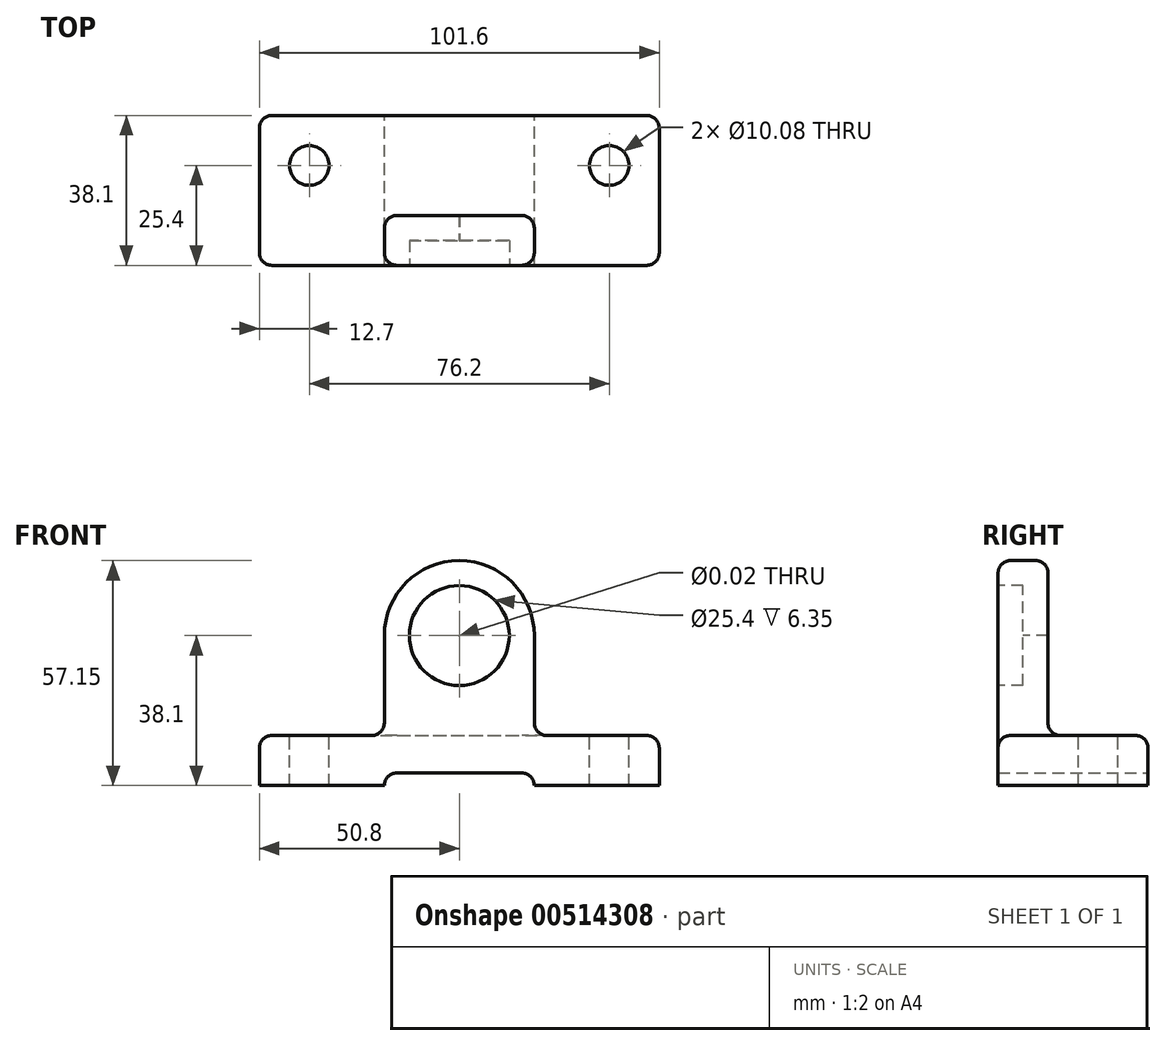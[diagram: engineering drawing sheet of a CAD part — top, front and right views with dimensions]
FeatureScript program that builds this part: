
annotation { "Feature Type Name" : "Feature", "Feature Type Description" : "" }
export const myFeature = defineFeature(function(context is Context, id is Id, definition is map)
    precondition{}
    {
        {
            var Q0;
            Q0=qCreatedBy(makeId("Top.planeOp"),FACE);
            var sketch = newSketch(context, id + "F0", { "sketchPlane" : qUnion([Q0])});
            skLineSegment(sketch, "E0.bottom", {"start": v(0, 0) * mm, "end": v(101.6, 0) * mm});
            skLineSegment(sketch, "E0.top", {"start": v(0, 38.1) * mm, "end": v(101.6, 38.1) * mm});
            skLineSegment(sketch, "E0.left", {"start": v(0, 0) * mm, "end": v(0, 38.1) * mm});
            skLineSegment(sketch, "E0.right", {"start": v(101.6, 0) * mm, "end": v(101.6, 38.1) * mm});
            skSolve(sketch);
        }
        {
            var Q0;
            Q0=makeQuery(id+"F0.imprint","IMPRINT",FACE,{"disambiguationData":[TD([[makeQuery(id+"F0.imprint","IMPRINT",EDGE,{"derivedFrom":sQuery(id+"F0.wireOp",EDGE,"E0.bottom")}),1.0]])]});
            extrude(context, id + "F1", {"entities" : qUnion([Q0]), "depth" : 12.7 * mm, "offsetDistance" : 25.4 * mm});
        }
        {
            var Q0;
            Q0=makeQuery(id+"F1.opExtrude","SWEPT_FACE",FACE,{"disambiguationData":[OSD([sQuery(id+"F0.wireOp",EDGE,"E0.bottom")])]});
            var sketch = newSketch(context, id + "F2", { "sketchPlane" : qUnion([Q0])});
            skLineSegment(sketch, "E1", {"start": v(31.75, 0) * mm, "end": v(31.75, 38.1) * mm});
            skArc(sketch, "E2", {"start": v(69.85, 38.1) * mm, "mid": v(50.8, 57.15) * mm, "end": v(31.75, 38.1) * mm});
            skLineSegment(sketch, "E3", {"start": v(69.85, 38.1) * mm, "end": v(69.85, 0) * mm});
            skLineSegment(sketch, "E4", {"start": v(69.85, 0) * mm, "end": v(31.75, 0) * mm});
            skLineSegment(sketch, "E5", {"start": v(50.8, 0) * mm, "end": v(50.8, 74) * mm, "construction": true});
            skPoint(sketch, "E5.endSnap0", {"position": v(50.8, 57.15) * mm});
            skLineSegment(sketch, "E6", {"start": v(50.8, 0) * mm, "end": v(0, 0) * mm, "construction": true});
            skSolve(sketch);
        }
        {
            var Q0;
            {var subQ0=sQuery(id+"F2.wireOp",EDGE,"E2");Q0=makeQuery(id+"F2.imprint","IMPRINT",FACE,{"disambiguationData":[TD([[makeQuery(id+"F2.imprint","IMPRINT",EDGE,{"derivedFrom":subQ0}),1.0]])]});}
            var Q1;
            {var subQ0=sQuery(id+"F2.wireOp",EDGE,"E4");Q1=makeQuery(id+"F2.imprint","IMPRINT",FACE,{"disambiguationData":[TD([[makeQuery(id+"F2.imprint","IMPRINT",EDGE,{"derivedFrom":subQ0}),1.0]])]});}
            extrude(context, id + "F3", {"entities" : qUnion([Q0, Q1]), "operationType" : NewBodyOperationType.ADD, "oppositeDirection" : true, "depth" : 12.7 * mm, "offsetDistance" : 25.4 * mm});
        }
        {
            var Q0;
            Q0=sQuery(id+"F2.wireOp",VERTEX,"E2.center");
            var Q1;
            Q1=makeQuery(id+"F1.opExtrude","SWEPT_BODY",BODY,{"disambiguationData":[OSD([sQuery(id+"F0.wireOp",EDGE,"E0.bottom"),sQuery(id+"F0.wireOp",EDGE,"E0.top"),sQuery(id+"F0.wireOp",EDGE,"E0.left"),sQuery(id+"F0.wireOp",EDGE,"E0.right")])]});
            hole(context, id + "F4", {"style" : HoleStyle.C_BORE, "endStyle" : HoleEndStyle.THROUGH, "standardTappedOrClearance" : lookupTablePath({ "standard" : "ANSI", "size" : "15/32 (0.47)", "type" : "Drilled" }), "standardBlindInLast" : lookupTablePath({ "standard" : "ANSI", "size" : "15/32", "type" : "Drilled" }), "holeDiameter" : 15 / 812.8 * mm, "cBoreDiameter" : 25.4 * mm, "cBoreDepth" : 6.35 * mm, "isTappedThrough" : true, "tappedDepth" : 12.7 * mm, "tapClearance" : 3, "locations" : qUnion([Q0]), "scope" : qUnion([Q1])});
        }
        {
            var Q0;
            Q0=makeQuery(id+"F1.opExtrude","SWEPT_FACE",FACE,{"disambiguationData":[OSD([sQuery(id+"F0.wireOp",EDGE,"E0.top")])]});
            var sketch = newSketch(context, id + "F5", { "sketchPlane" : qUnion([Q0])});
            skLineSegment(sketch, "E7", {"start": v(-69.85, 0) * mm, "end": v(-69.85, 3.18) * mm});
            skLineSegment(sketch, "E8", {"start": v(-69.85, 3.18) * mm, "end": v(-31.75, 3.18) * mm});
            skLineSegment(sketch, "E9", {"start": v(-31.75, 3.18) * mm, "end": v(-31.75, 0) * mm});
            skLineSegment(sketch, "E10", {"start": v(-69.85, 0) * mm, "end": v(-31.75, 0) * mm});
            skSolve(sketch);
        }
        {
            var Q0;
            Q0=makeQuery(id+"F5.imprint","IMPRINT",FACE,{"disambiguationData":[TD([[makeQuery(id+"F5.imprint","IMPRINT",EDGE,{"derivedFrom":sQuery(id+"F5.wireOp",EDGE,"E7")}),-1.0]])]});
            extrude(context, id + "F6", {"entities" : qUnion([Q0]), "operationType" : NewBodyOperationType.REMOVE, "endBound" : BoundingType.THROUGH_ALL, "oppositeDirection" : true, "depth" : 25.4 * mm, "offsetDistance" : 25.4 * mm});
        }
        {
            var Q0;
            Q0=makeQuery(id+"F1.opExtrude","CAP_FACE",FACE,{"disambiguationData":[OSD([sQuery(id+"F0.wireOp",EDGE,"E0.bottom"),sQuery(id+"F0.wireOp",EDGE,"E0.top"),sQuery(id+"F0.wireOp",EDGE,"E0.left"),sQuery(id+"F0.wireOp",EDGE,"E0.right")])],"isStart":false});
            var sketch = newSketch(context, id + "F7", { "sketchPlane" : qUnion([Q0])});
            skLineSegment(sketch, "E11.bottom", {"start": v(0, 38.1) * mm, "end": v(12.7, 38.1) * mm, "construction": true});
            skLineSegment(sketch, "E11.top", {"start": v(0, 25.4) * mm, "end": v(12.7, 25.4) * mm, "construction": true});
            skLineSegment(sketch, "E11.left", {"start": v(0, 38.1) * mm, "end": v(0, 25.4) * mm, "construction": true});
            skLineSegment(sketch, "E11.right", {"start": v(12.7, 38.1) * mm, "end": v(12.7, 25.4) * mm, "construction": true});
            skLineSegment(sketch, "E12.bottom", {"start": v(101.6, 38.1) * mm, "end": v(88.9, 38.1) * mm, "construction": true});
            skLineSegment(sketch, "E12.top", {"start": v(101.6, 25.4) * mm, "end": v(88.9, 25.4) * mm, "construction": true});
            skLineSegment(sketch, "E12.left", {"start": v(101.6, 38.1) * mm, "end": v(101.6, 25.4) * mm, "construction": true});
            skLineSegment(sketch, "E12.right", {"start": v(88.9, 38.1) * mm, "end": v(88.9, 25.4) * mm, "construction": true});
            skSolve(sketch);
        }
        {
            var Q0;
            Q0=sQuery(id+"F7.wireOp",VERTEX,"E11.right.end");
            var Q1;
            Q1=sQuery(id+"F7.wireOp",VERTEX,"E12.right.end");
            var Q2;
            Q2=makeQuery(id+"F1.opExtrude","SWEPT_BODY",BODY,{"disambiguationData":[OSD([sQuery(id+"F0.wireOp",EDGE,"E0.bottom"),sQuery(id+"F0.wireOp",EDGE,"E0.top"),sQuery(id+"F0.wireOp",EDGE,"E0.left"),sQuery(id+"F0.wireOp",EDGE,"E0.right")])]});
            hole(context, id + "F8", {"style" : HoleStyle.SIMPLE, "endStyle" : HoleEndStyle.THROUGH, "standardTappedOrClearance" : lookupTablePath({ "standard" : "ANSI", "fit" : "Normal (ASME)", "size" : "3/8", "type" : "Clearance" }), "standardBlindInLast" : lookupTablePath({ "fit" : "Free", "standard" : "ANSI", "size" : "3/8", "type" : "Clearance" }), "holeDiameter" : 10.08 * mm, "isTappedThrough" : true, "tappedDepth" : 12.7 * mm, "tapClearance" : 3, "locations" : qUnion([Q0, Q1]), "scope" : qUnion([Q2])});
        }
        {
            var Q0;
            Q0=makeQuery(id+"F1.opExtrude","SWEPT_EDGE",EDGE,{"disambiguationData":[OSD([sQuery(id+"F0.wireOp",EDGE,"E0.bottom"),sQuery(id+"F0.wireOp",EDGE,"E0.left")])]});
            var Q1;
            Q1=makeQuery(id+"F1.opExtrude","SWEPT_EDGE",EDGE,{"disambiguationData":[OSD([sQuery(id+"F0.wireOp",EDGE,"E0.bottom"),sQuery(id+"F0.wireOp",EDGE,"E0.right")])]});
            var Q2;
            Q2=makeQuery(id+"F1.opExtrude","SWEPT_EDGE",EDGE,{"disambiguationData":[OSD([sQuery(id+"F0.wireOp",EDGE,"E0.top"),sQuery(id+"F0.wireOp",EDGE,"E0.right")])]});
            var Q3;
            Q3=makeQuery(id+"F1.opExtrude","SWEPT_EDGE",EDGE,{"disambiguationData":[OSD([sQuery(id+"F0.wireOp",EDGE,"E0.top"),sQuery(id+"F0.wireOp",EDGE,"E0.left")])]});
            var Q4;
            Q4=makeQuery(id+"F6.boolean.opBoolean","COPY",EDGE,{"derivedFrom":makeQuery(id+"F6.opExtrude","SWEPT_EDGE",EDGE,{"disambiguationData":[OSD([sQuery(id+"F5.wireOp",EDGE,"E8"),sQuery(id+"F5.wireOp",EDGE,"E9")])]})});
            var Q5;
            Q5=makeQuery(id+"F6.boolean.opBoolean","COPY",EDGE,{"derivedFrom":makeQuery(id+"F6.opExtrude","SWEPT_EDGE",EDGE,{"disambiguationData":[OSD([sQuery(id+"F5.wireOp",EDGE,"E7"),sQuery(id+"F5.wireOp",EDGE,"E8")])]})});
            fillet(context, id + "F9", {"entities" : qUnion([Q0, Q1, Q2, Q3, Q4, Q5]), "radius" : 3.17 * mm, "tangentPropagation" : true, "allowEdgeOverflow" : false});
        }
        {
            var Q0;
            Q0=makeQuery(id+"F3.opExtrude","CAP_EDGE",EDGE,{"disambiguationData":[OSD([sQuery(id+"F2.wireOp",EDGE,"E2")])],"isStart":true});
            var Q1;
            Q1=makeQuery(id+"F3.opExtrude","CAP_EDGE",EDGE,{"disambiguationData":[OSD([sQuery(id+"F2.wireOp",EDGE,"E2")])],"isStart":false});
            var Q2;
            Q2=makeQuery(id+"F3.opExtrude","CAP_EDGE",EDGE,{"disambiguationData":[OSD([sQuery(id+"F2.wireOp",EDGE,"E1")])],"isStart":true});
            var Q3;
            Q3=makeQuery(id+"F3.opExtrude","CAP_EDGE",EDGE,{"disambiguationData":[OSD([sQuery(id+"F2.wireOp",EDGE,"E3")])],"isStart":true});
            var Q4;
            Q4=makeQuery(id+"F3.opExtrude","CAP_EDGE",EDGE,{"disambiguationData":[OSD([sQuery(id+"F2.wireOp",EDGE,"E1")])],"isStart":false});
            var Q5;
            {var subQ1=sQuery(id+"F0.wireOp",EDGE,"E0.left");var subQ2=sQuery(id+"F0.wireOp",EDGE,"E0.bottom");Q5=makeQuery(id+"F3.boolean.opBoolean","SPLIT",EDGE,{"disambiguationData":[TD([makeQuery(id+"F1.opExtrude","SWEPT_FACE",FACE,{"disambiguationData":[OSD([subQ1])]})])],"derivedFrom":makeQuery(id+"F1.opExtrude","CAP_EDGE",EDGE,{"disambiguationData":[OSD([subQ2])],"isStart":false})});}
            var Q6;
            {var subQ0=sQuery(id+"F0.wireOp",EDGE,"E0.left");var subQ1=sQuery(id+"F0.wireOp",EDGE,"E0.bottom");Q6=makeQuery(id+"F9.opFillet","BLEND_EDGE",EDGE,{"blendedFrom":[makeQuery(id+"F1.opExtrude","SWEPT_EDGE",EDGE,{"disambiguationData":[OSD([subQ1,subQ0])]}),makeQuery(id+"F1.opExtrude","CAP_FACE",FACE,{"disambiguationData":[OSD([subQ1,sQuery(id+"F0.wireOp",EDGE,"E0.top"),subQ0,sQuery(id+"F0.wireOp",EDGE,"E0.right")])],"isStart":false})],"blendedInto":[makeQuery(id+"F1.opExtrude","CAP_FACE",FACE,{"disambiguationData":[OSD([subQ1,sQuery(id+"F0.wireOp",EDGE,"E0.top"),subQ0,sQuery(id+"F0.wireOp",EDGE,"E0.right")])],"isStart":false})]});}
            var Q7;
            Q7=makeQuery(id+"F1.opExtrude","CAP_EDGE",EDGE,{"disambiguationData":[OSD([sQuery(id+"F0.wireOp",EDGE,"E0.left")])],"isStart":false});
            var Q8;
            {var subQ0=sQuery(id+"F0.wireOp",EDGE,"E0.left");var subQ1=sQuery(id+"F0.wireOp",EDGE,"E0.top");Q8=makeQuery(id+"F9.opFillet","BLEND_EDGE",EDGE,{"blendedFrom":[makeQuery(id+"F1.opExtrude","SWEPT_EDGE",EDGE,{"disambiguationData":[OSD([subQ1,subQ0])]}),makeQuery(id+"F1.opExtrude","CAP_FACE",FACE,{"disambiguationData":[OSD([sQuery(id+"F0.wireOp",EDGE,"E0.bottom"),subQ1,subQ0,sQuery(id+"F0.wireOp",EDGE,"E0.right")])],"isStart":false})],"blendedInto":[makeQuery(id+"F1.opExtrude","CAP_FACE",FACE,{"disambiguationData":[OSD([sQuery(id+"F0.wireOp",EDGE,"E0.bottom"),subQ1,subQ0,sQuery(id+"F0.wireOp",EDGE,"E0.right")])],"isStart":false})]});}
            var Q9;
            Q9=makeQuery(id+"F1.opExtrude","CAP_EDGE",EDGE,{"disambiguationData":[OSD([sQuery(id+"F0.wireOp",EDGE,"E0.top")])],"isStart":false});
            var Q10;
            {var subQ0=sQuery(id+"F0.wireOp",EDGE,"E0.right");var subQ1=sQuery(id+"F0.wireOp",EDGE,"E0.top");Q10=makeQuery(id+"F9.opFillet","BLEND_EDGE",EDGE,{"blendedFrom":[makeQuery(id+"F1.opExtrude","SWEPT_EDGE",EDGE,{"disambiguationData":[OSD([subQ1,subQ0])]}),makeQuery(id+"F1.opExtrude","CAP_FACE",FACE,{"disambiguationData":[OSD([sQuery(id+"F0.wireOp",EDGE,"E0.bottom"),subQ1,sQuery(id+"F0.wireOp",EDGE,"E0.left"),subQ0])],"isStart":false})],"blendedInto":[makeQuery(id+"F1.opExtrude","CAP_FACE",FACE,{"disambiguationData":[OSD([sQuery(id+"F0.wireOp",EDGE,"E0.bottom"),subQ1,sQuery(id+"F0.wireOp",EDGE,"E0.left"),subQ0])],"isStart":false})]});}
            var Q11;
            Q11=makeQuery(id+"F1.opExtrude","CAP_EDGE",EDGE,{"disambiguationData":[OSD([sQuery(id+"F0.wireOp",EDGE,"E0.right")])],"isStart":false});
            var Q12;
            {var subQ0=sQuery(id+"F0.wireOp",EDGE,"E0.right");var subQ1=sQuery(id+"F0.wireOp",EDGE,"E0.bottom");Q12=makeQuery(id+"F9.opFillet","BLEND_EDGE",EDGE,{"blendedFrom":[makeQuery(id+"F1.opExtrude","SWEPT_EDGE",EDGE,{"disambiguationData":[OSD([subQ1,subQ0])]}),makeQuery(id+"F1.opExtrude","CAP_FACE",FACE,{"disambiguationData":[OSD([subQ1,sQuery(id+"F0.wireOp",EDGE,"E0.top"),sQuery(id+"F0.wireOp",EDGE,"E0.left"),subQ0])],"isStart":false})],"blendedInto":[makeQuery(id+"F1.opExtrude","CAP_FACE",FACE,{"disambiguationData":[OSD([subQ1,sQuery(id+"F0.wireOp",EDGE,"E0.top"),sQuery(id+"F0.wireOp",EDGE,"E0.left"),subQ0])],"isStart":false})]});}
            var Q13;
            {var subQ1=sQuery(id+"F0.wireOp",EDGE,"E0.right");var subQ2=sQuery(id+"F0.wireOp",EDGE,"E0.bottom");Q13=makeQuery(id+"F3.boolean.opBoolean","SPLIT",EDGE,{"disambiguationData":[TD([makeQuery(id+"F1.opExtrude","SWEPT_FACE",FACE,{"disambiguationData":[OSD([subQ1])]})])],"derivedFrom":makeQuery(id+"F1.opExtrude","CAP_EDGE",EDGE,{"disambiguationData":[OSD([subQ2])],"isStart":false})});}
            var Q14;
            Q14=makeQuery(id+"F3.boolean.opBoolean","INTERSECT",EDGE,{"derivedFrom":[makeQuery(id+"F1.opExtrude","CAP_FACE",FACE,{"disambiguationData":[OSD([sQuery(id+"F0.wireOp",EDGE,"E0.bottom"),sQuery(id+"F0.wireOp",EDGE,"E0.top"),sQuery(id+"F0.wireOp",EDGE,"E0.left"),sQuery(id+"F0.wireOp",EDGE,"E0.right")])],"isStart":false}),makeQuery(id+"F3.opExtrude","CAP_FACE",FACE,{"disambiguationData":[OSD([sQuery(id+"F2.wireOp",EDGE,"E1"),sQuery(id+"F2.wireOp",EDGE,"E2"),sQuery(id+"F2.wireOp",EDGE,"E3"),sQuery(id+"F2.wireOp",EDGE,"E4")])],"isStart":false})]});
            var Q15;
            Q15=makeQuery(id+"F3.boolean.opBoolean","INTERSECT",EDGE,{"derivedFrom":[makeQuery(id+"F1.opExtrude","CAP_FACE",FACE,{"disambiguationData":[OSD([sQuery(id+"F0.wireOp",EDGE,"E0.bottom"),sQuery(id+"F0.wireOp",EDGE,"E0.top"),sQuery(id+"F0.wireOp",EDGE,"E0.left"),sQuery(id+"F0.wireOp",EDGE,"E0.right")])],"isStart":false}),makeQuery(id+"F3.opExtrude","SWEPT_FACE",FACE,{"disambiguationData":[OSD([sQuery(id+"F2.wireOp",EDGE,"E1")])]})]});
            var Q16;
            Q16=makeQuery(id+"F3.opExtrude","CAP_EDGE",EDGE,{"disambiguationData":[OSD([sQuery(id+"F2.wireOp",EDGE,"E3")])],"isStart":false});
            var Q17;
            Q17=makeQuery(id+"F3.boolean.opBoolean","INTERSECT",EDGE,{"derivedFrom":[makeQuery(id+"F1.opExtrude","CAP_FACE",FACE,{"disambiguationData":[OSD([sQuery(id+"F0.wireOp",EDGE,"E0.bottom"),sQuery(id+"F0.wireOp",EDGE,"E0.top"),sQuery(id+"F0.wireOp",EDGE,"E0.left"),sQuery(id+"F0.wireOp",EDGE,"E0.right")])],"isStart":false}),makeQuery(id+"F3.opExtrude","SWEPT_FACE",FACE,{"disambiguationData":[OSD([sQuery(id+"F2.wireOp",EDGE,"E3")])]})]});
            fillet(context, id + "F10", {"entities" : qUnion([Q0, Q1, Q2, Q3, Q4, Q5, Q6, Q7, Q8, Q9, Q10, Q11, Q12, Q13, Q14, Q15, Q16, Q17]), "radius" : 3.17 * mm, "tangentPropagation" : true, "allowEdgeOverflow" : false});
        }
    });
